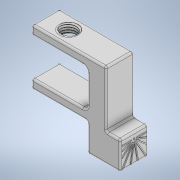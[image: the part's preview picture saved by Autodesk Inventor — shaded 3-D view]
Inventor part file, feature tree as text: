
AUTODESK INVENTOR PART (.ipt)
format: ipt  version: 2020 (Build 240168000, 168)  size: 770,560 bytes
history: native  units: mm
features: sketch x12, extrude x10, fillet x2, thread x1, revolve x1, helix x1
ambient origin geometry x8: Origin, YZ Plane, XZ Plane, XY Plane, X Axis, Y Axis, Z Axis, Center Point
bodies: Solid1 (feature_tree), Solid4 (feature_tree)
feature tree (27):
  extrude  "Extrusion1"  Depth=30.0mm
  extrude  "Extrusion2"  Depth=60.0mm
  extrude  "Extrusion3"  Depth=80.0mm TaperAngle=0.0deg
  extrude  "Extrusion4"  Depth=30.0mm
  fillet  "Fillet1"  Radius=20.0mm
  extrude  "Extrusion12"  Depth=10.0mm TaperAngle=0.0deg
  extrude  "Extrusion13"  Depth=9.599311mm
  extrude  "Extrusion14"  Depth=15.0mm TaperAngle=0.0deg
  thread  "Thread8"  [1 undecoded]
  revolve  "Revolution4"  [1 undecoded]
  helix  "Coil3"  [1 undecoded]
  fillet  "Fillet2"  Radius=2.5mm
  extrude  "Extrusion23"  TaperAngle=0.0deg  [1 undecoded]
  extrude  "Extrusion35"  Depth=10.0mm
  extrude  "Extrusion36"  Depth=9.599311mm
  sketch  "Sketch2"  dims[d0=60.0mm d1=30.0mm]
  sketch  "Sketch3"  dims[d2=80.0mm d3=0.0mm d4=60.0mm]
  sketch  "Sketch4"  dims[d5=40.0mm d6=80.0mm d7=0.0mm]
  sketch  "Sketch5"  dims[d8=20.0mm d9=30.0mm d10=20.0mm d11=0.0mm]
  sketch  "Sketch23"  dims[d12=20.0mm d13=10.0mm d14=0.0mm]
  sketch  "Sketch24"  dims[d17=5.0mm d55=9.599311mm]
  sketch  "Sketch25"  dims[d76=9.599311mm d91=15.0mm d92=0.0mm d93=5.0mm d94=0.0mm]
  sketch  "Sketch29"  dims[d95=5.0mm d96=0.0mm d103=10.0mm d104=0.0mm d105=9.599311mm d106=0.400208mm d107=0.400208mm d110=2.5mm]
  sketch  "Sketch30"  dims[d112=9.599311mm d114=0.0mm]
  sketch  "Sketch49"  dims[d115=2.5025mm d116=15.0mm d117=10.0mm d118=0.0mm d119=0.0mm d120=0.0mm d121=0.0mm d122=0.0mm d141=9.599311mm]
  sketch  "Sketch67"  dims[d166=9.599311mm d186=9.599311mm]
  sketch  "Sketch68"  dims[d197=2.0mm d207=9.599311mm d227=9.599311mm d250=9.599311mm d279=1.05mm d280=1.05mm d281=1.05mm d282=1.05mm d283=1.05mm d284=1.05mm d285=1.05mm d286=1.05mm d287=6.9mm d288=0.0mm d1059=2.0mm d1060=9.0mm d1061=0.0mm d1069=30.0mm d1074=30.0mm d1110=30.0mm d1113=30.0mm d1120=7.759mm d1121=0.7mm d1122=0.0mm d271=0.5mm d272=0.872665mm d273=0.5mm d274=0.872665mm]
note: 4 required parameter values undecoded (feature->parameter linkage not recoverable at this tier; creation-order binding heuristic only, values carry confidence <= 0.55)